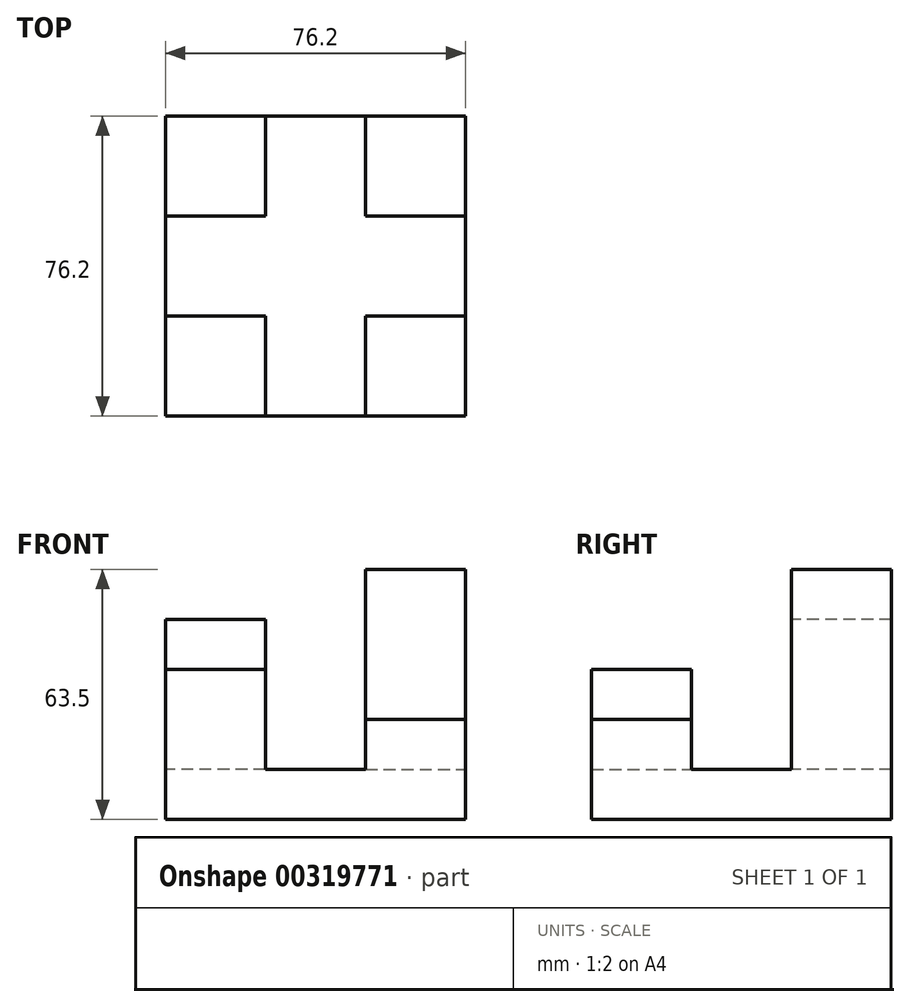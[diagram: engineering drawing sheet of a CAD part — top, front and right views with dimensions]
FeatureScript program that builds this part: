
annotation { "Feature Type Name" : "Feature", "Feature Type Description" : "" }
export const myFeature = defineFeature(function(context is Context, id is Id, definition is map)
    precondition{}
    {
        {
            var Q0;
            Q0=qCreatedBy(makeId("Right.planeOp"),FACE);
            var sketch = newSketch(context, id + "F0", { "sketchPlane" : qUnion([Q0])});
            skLineSegment(sketch, "E0", {"start": v(-35.94, -44.02) * mm, "end": v(40.26, -44.02) * mm});
            skLineSegment(sketch, "E1", {"start": v(40.26, -44.02) * mm, "end": v(40.26, -31.32) * mm});
            skLineSegment(sketch, "E2", {"start": v(40.26, -31.32) * mm, "end": v(-35.94, -31.32) * mm});
            skLineSegment(sketch, "E3", {"start": v(-35.94, -31.32) * mm, "end": v(-35.94, -44.02) * mm});
            skSolve(sketch);
        }
        {
            var Q0;
            Q0=makeQuery(id+"F0.imprint","IMPRINT",FACE,{"disambiguationData":[TD([[makeQuery(id+"F0.imprint","IMPRINT",EDGE,{"derivedFrom":sQuery(id+"F0.wireOp",EDGE,"E0")}),1.0]])]});
            extrude(context, id + "F1", {"entities" : qUnion([Q0]), "oppositeDirection" : true, "depth" : 76.2 * mm});
        }
        {
            var Q0;
            Q0=makeQuery(id+"F1.opExtrude","SWEPT_FACE",FACE,{"disambiguationData":[OSD([sQuery(id+"F0.wireOp",EDGE,"E2")])]});
            var sketch = newSketch(context, id + "F2", { "sketchPlane" : qUnion([Q0])});
            skLineSegment(sketch, "E4", {"start": v(0, -35.94) * mm, "end": v(-25.4, -35.94) * mm});
            skLineSegment(sketch, "E5", {"start": v(-25.4, -35.94) * mm, "end": v(-25.4, -10.54) * mm});
            skLineSegment(sketch, "E6", {"start": v(-25.4, -10.54) * mm, "end": v(0, -10.54) * mm});
            skLineSegment(sketch, "E7", {"start": v(0, -10.54) * mm, "end": v(0, -35.94) * mm});
            skLineSegment(sketch, "E8", {"start": v(-76.2, -35.94) * mm, "end": v(-50.8, -35.94) * mm});
            skLineSegment(sketch, "E9", {"start": v(-50.8, -35.94) * mm, "end": v(-50.8, -10.54) * mm});
            skLineSegment(sketch, "E10", {"start": v(-50.8, -10.54) * mm, "end": v(-76.2, -10.54) * mm});
            skLineSegment(sketch, "E11", {"start": v(-76.2, -10.54) * mm, "end": v(-76.2, -35.94) * mm});
            skLineSegment(sketch, "E12", {"start": v(-76.2, 40.26) * mm, "end": v(-50.8, 40.26) * mm});
            skLineSegment(sketch, "E13", {"start": v(-50.8, 40.26) * mm, "end": v(-50.8, 14.86) * mm});
            skLineSegment(sketch, "E14", {"start": v(-50.8, 14.86) * mm, "end": v(-76.2, 14.86) * mm});
            skLineSegment(sketch, "E15", {"start": v(-76.2, 14.86) * mm, "end": v(-76.2, 40.26) * mm});
            skLineSegment(sketch, "E16", {"start": v(0, 40.26) * mm, "end": v(-25.4, 40.26) * mm});
            skLineSegment(sketch, "E17", {"start": v(-25.4, 40.26) * mm, "end": v(-25.4, 14.86) * mm});
            skLineSegment(sketch, "E18", {"start": v(-25.4, 14.86) * mm, "end": v(0, 14.86) * mm});
            skLineSegment(sketch, "E19", {"start": v(0, 14.86) * mm, "end": v(0, 40.26) * mm});
            skSolve(sketch);
        }
        {
            var Q0;
            Q0=makeQuery(id+"F2.imprint","IMPRINT",FACE,{"disambiguationData":[TD([[makeQuery(id+"F2.imprint","IMPRINT",EDGE,{"derivedFrom":sQuery(id+"F2.wireOp",EDGE,"E4")}),1.0]])]});
            var Q1;
            Q1=makeQuery(id+"F2.imprint","IMPRINT",FACE,{"disambiguationData":[TD([[makeQuery(id+"F2.imprint","IMPRINT",EDGE,{"derivedFrom":sQuery(id+"F2.wireOp",EDGE,"E8")}),1.0]])]});
            var Q2;
            Q2=makeQuery(id+"F2.imprint","IMPRINT",FACE,{"disambiguationData":[TD([[makeQuery(id+"F2.imprint","IMPRINT",EDGE,{"derivedFrom":sQuery(id+"F2.wireOp",EDGE,"E16")}),-1.0]])]});
            var Q3;
            Q3=makeQuery(id+"F2.imprint","IMPRINT",FACE,{"disambiguationData":[TD([[makeQuery(id+"F2.imprint","IMPRINT",EDGE,{"derivedFrom":sQuery(id+"F2.wireOp",EDGE,"E12")}),-1.0]])]});
            extrude(context, id + "F3", {"entities" : qUnion([Q0, Q1, Q2, Q3]), "operationType" : NewBodyOperationType.ADD, "depth" : 12.7 * mm});
        }
        {
            var Q0;
            Q0=makeQuery(id+"F3.opExtrude","CAP_FACE",FACE,{"disambiguationData":[OSD([sQuery(id+"F2.wireOp",EDGE,"E8"),sQuery(id+"F2.wireOp",EDGE,"E9"),sQuery(id+"F2.wireOp",EDGE,"E10"),sQuery(id+"F2.wireOp",EDGE,"E11")])],"isStart":false});
            extrude(context, id + "F4", {"entities" : qUnion([Q0]), "operationType" : NewBodyOperationType.ADD, "depth" : 12.7 * mm});
        }
        {
            var Q0;
            Q0=makeQuery(id+"F3.opExtrude","CAP_FACE",FACE,{"disambiguationData":[OSD([sQuery(id+"F2.wireOp",EDGE,"E16"),sQuery(id+"F2.wireOp",EDGE,"E17"),sQuery(id+"F2.wireOp",EDGE,"E18"),sQuery(id+"F2.wireOp",EDGE,"E19")])],"isStart":false});
            extrude(context, id + "F5", {"entities" : qUnion([Q0]), "operationType" : NewBodyOperationType.ADD, "depth" : 38.1 * mm});
        }
        {
            var Q0;
            Q0=makeQuery(id+"F3.opExtrude","CAP_FACE",FACE,{"disambiguationData":[OSD([sQuery(id+"F2.wireOp",EDGE,"E12"),sQuery(id+"F2.wireOp",EDGE,"E13"),sQuery(id+"F2.wireOp",EDGE,"E14"),sQuery(id+"F2.wireOp",EDGE,"E15")])],"isStart":false});
            extrude(context, id + "F6", {"entities" : qUnion([Q0]), "operationType" : NewBodyOperationType.ADD, "depth" : 25.4 * mm});
        }
    });
